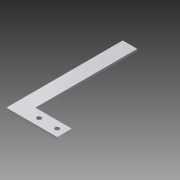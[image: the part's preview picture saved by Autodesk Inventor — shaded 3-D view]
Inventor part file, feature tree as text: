
AUTODESK INVENTOR PART (.ipt)
format: ipt  version: 2015 (Build 190159000, 159)  size: 126,976 bytes
history: native  units: mm
features: sketch x6, extrude x4, hole x2, other x1
ambient origin geometry x8: Origin, YZ Plane, XZ Plane, XY Plane, X Axis, Y Axis, Z Axis, Center Point
bodies: Body1 (feature_tree)
feature tree (13):
  other  "ソリッド1"
  extrude  "押し出し1"  Depth=70.0mm
  extrude  "押し出し2"  Depth=50.0mm
  hole  "穴1"  [1 undecoded]
  hole  "穴2"  [1 undecoded]
  extrude  "押し出し4"  Depth=10.0mm
  extrude  "押し出し5"  Depth=10.0mm
  sketch  "スケッチ1"
  sketch  "スケッチ2"
  sketch  "スケッチ3"
  sketch  "スケッチ5"
  sketch  "スケッチ6"
  sketch  "スケッチ7"
note: 2 required parameter values undecoded (feature->parameter linkage not recoverable at this tier; creation-order binding heuristic only, values carry confidence <= 0.55)
